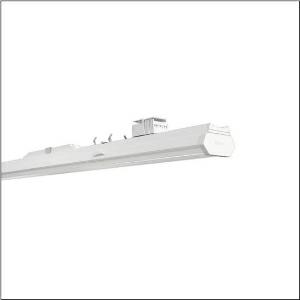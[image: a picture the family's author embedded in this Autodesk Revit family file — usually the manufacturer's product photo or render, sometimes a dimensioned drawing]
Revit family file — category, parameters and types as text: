
# Revit family: licross_11_protected_ho_51tp11mn4gxs
name_source: partatom
category: Lighting Fixtures
units: mm (PartAtom-declared; Revit-internal decimal feet)

## family parameters
Cut with Voids When Loaded = No
Host = Face
Light Source = No
Part Type = Normal
Room Calculation Point = No
Round Connector Dimension = Use Diameter
Shared = No

## types (1)
- --- (1 x LED, 16070 lm, 87.4 W, 4000K)
    Apparent Load = 87 VA
    CIE Flux Codes = 84 94 98 99 100
    Color Rendering = 80
    Color Temperature = 4000K
    Default Elevation = 1800 mm
    Description = Licross 11 Protected HO, luminaire insert, of sheet steel, galvanised, coil coated, white, length: 1.500mm, width: 90mm, height: 101mm, LED rated luminous flux: 16.070lm, light colour: 840, SDCM (Standard Deviation of Colour Matching)MacAdam ≤ 2 SDCM (initial), control gear: ON/OFF Multilumen, with plug, 3-pole, with phase selection, mains connection: 220..240V, AC, 50/60Hz, rated input power: 87W, internal wiring halogen-free, primary light control with lens, of plastic, primary optical cover: cover, of PMMA, light emission: direct distribution, primary light characteristic: symmetric, protection rating (complete): IP64, insulation class (complete): insulation class I (protective earthing), certification: CE, ENEC, VDE, UKCA, protection symbol: D if used in an environment with conductive dust loads with corresponding accessories, impact resistance: IK06, permissible ambient temperature for indoor applications: -35..+35°C, corresponds to IFS (International Featured Standards) requirements for safety and quality in the food industry, reducing of maximum allowable ambient temperature of 5°C with ceiling mounting, LABS conformity tested according to VDMA 24364:2018-05, The light source and the operating device comply with the requirements of the Ecodesign Regulation (EU) 2019/2020 and are replaceable in accordance with this regulation, packaging unit: 1 piece
    Height = 92 mm
    Lamp = 1 x LED
    Lamp Light Flux = 16070 lm
    Lamp Power = 87.4 W
    Lamp count = 1
    Length = 1500 mm
    Luminous efficacy = 184 lm/W
    Manufacturer = Siteco
    ModVariant = No
    Model = 51TP11MN4GXS
    Mounting Place = Ceiling
    Mounting Type = Pendant
    Number of Poles = 1
    OnlyDefault = Yes
    Power Factor = 1
    Product Name = Licross 11 Protected HO
    Product group = luminaire insert | ceiling pendant
    ProductGroupID = 901
    Protection Class = Protection class I
    Protection Degree = IP 64
    RLX_Detail_Level = 1
    RLX_Emergency_Light_Flux = 0 lm
    RLX_Emergency_Type = 0
    RLX_Emergency_Type_DB = No
    RlxData = <blob elided: 22261 chars, md5=1632420e>
    Socket = socket
    Standby Power = 0 W
    System Light Flux = 16070 lm
    System Power = 87 W
    Type Comments = factory setting: luminous flux: 100 % | (A | C | E) | 203 mA
    Type Image = l_1256148.jpg
    URL = http://relux.com
    VarID = @adj_090421
    Voltage = 0 V
    Weight = 0.00 kg
    Width = 88 mm

## geometry (parser evidence)
native form markers: Blend x4, Sweep x10
no freeform markers — native parametric forms only
